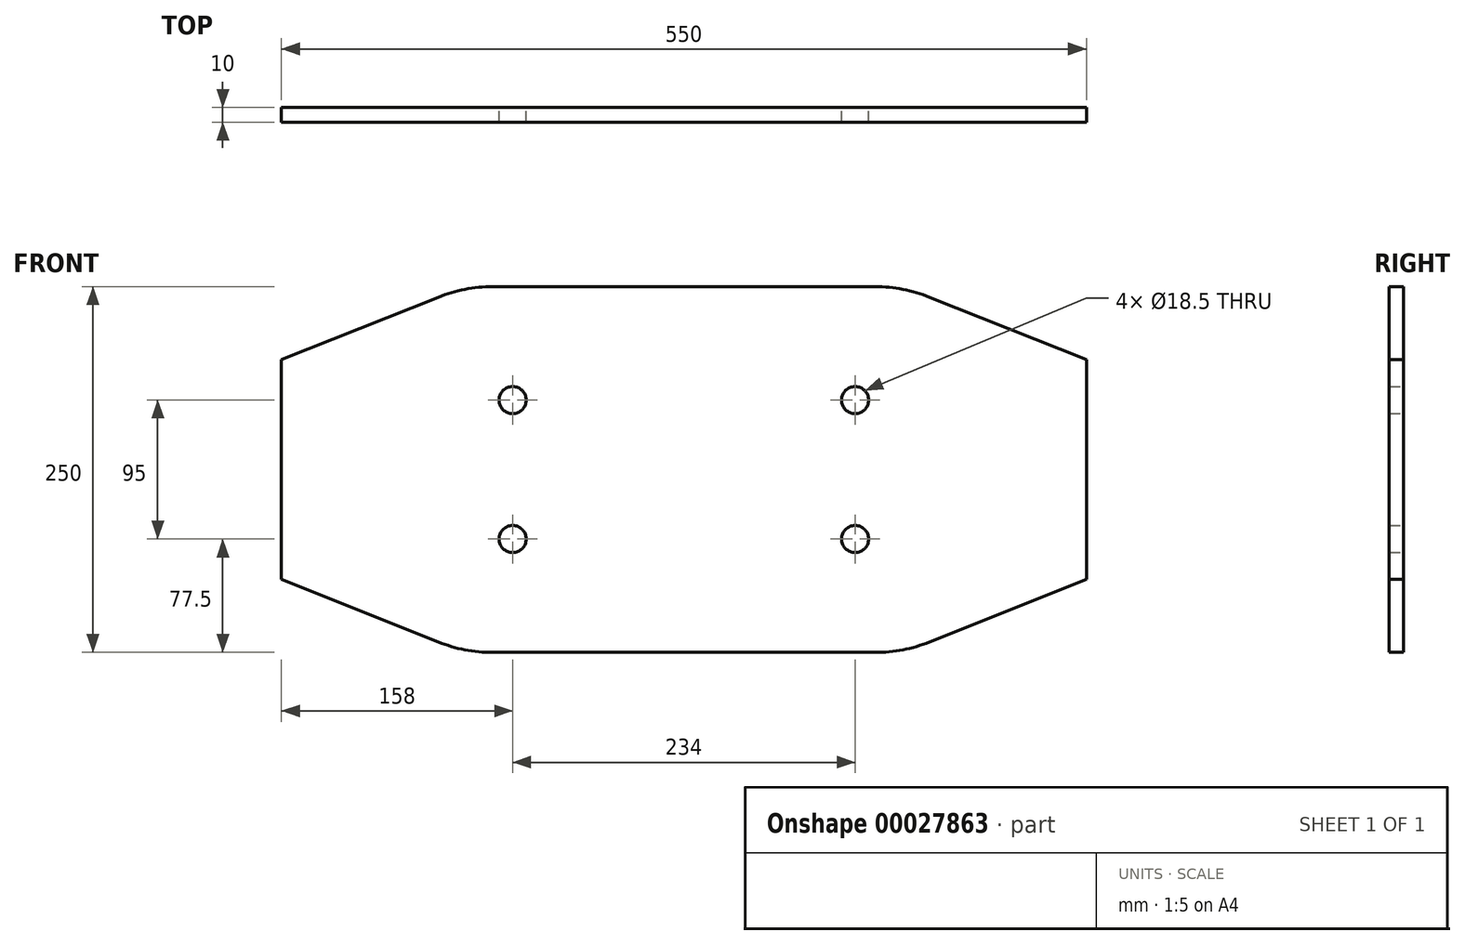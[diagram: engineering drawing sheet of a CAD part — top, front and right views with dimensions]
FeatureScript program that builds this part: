
annotation { "Feature Type Name" : "Feature", "Feature Type Description" : "" }
export const myFeature = defineFeature(function(context is Context, id is Id, definition is map)
    precondition{}
    {
        {
            var Q0;
            Q0=qCreatedBy(makeId("Front.planeOp"),FACE);
            var sketch = newSketch(context, id + "F0", { "sketchPlane" : qUnion([Q0])});
            skLineSegment(sketch, "E0", {"start": v(0, 0) * mm, "end": v(0, 150) * mm});
            skLineSegment(sketch, "E1", {"start": v(0, 150) * mm, "end": v(107.12, 192.85) * mm});
            skLineSegment(sketch, "E2", {"start": v(144.26, 200) * mm, "end": v(405.74, 200) * mm});
            skLineSegment(sketch, "E3", {"start": v(442.88, 192.85) * mm, "end": v(550, 150) * mm});
            skLineSegment(sketch, "E4", {"start": v(550, 150) * mm, "end": v(550, 0) * mm});
            skLineSegment(sketch, "E5", {"start": v(550, 0) * mm, "end": v(442.88, -42.85) * mm});
            skLineSegment(sketch, "E6", {"start": v(405.74, -50) * mm, "end": v(144.26, -50) * mm});
            skLineSegment(sketch, "E7", {"start": v(107.12, -42.85) * mm, "end": v(0, 0) * mm});
            skPoint(sketch, "E8.visualSharp", {"position": v(125, 200) * mm});
            skArc(sketch, "E8.filletArc", {"start": v(144.26, 200) * mm, "mid": v(125.35, 198.2) * mm, "end": v(107.12, 192.85) * mm});
            skPoint(sketch, "E9.visualSharp", {"position": v(425, 200) * mm});
            skArc(sketch, "E9.filletArc", {"start": v(442.88, 192.85) * mm, "mid": v(424.65, 198.2) * mm, "end": v(405.74, 200) * mm});
            skPoint(sketch, "E10.visualSharp", {"position": v(125, -50) * mm});
            skArc(sketch, "E10.filletArc", {"start": v(107.12, -42.85) * mm, "mid": v(125.35, -48.2) * mm, "end": v(144.26, -50) * mm});
            skPoint(sketch, "E11.visualSharp", {"position": v(425, -50) * mm});
            skArc(sketch, "E11.filletArc", {"start": v(405.74, -50) * mm, "mid": v(424.65, -48.2) * mm, "end": v(442.88, -42.85) * mm});
            skCircle(sketch, "E12", {"center": v(158, 122.5) * mm, "radius": 9.25 * mm});
            skCircle(sketch, "E13", {"center": v(158, 27.5) * mm, "radius": 9.25 * mm});
            skCircle(sketch, "E14", {"center": v(392, 122.5) * mm, "radius": 9.25 * mm});
            skCircle(sketch, "E15", {"center": v(392, 27.5) * mm, "radius": 9.25 * mm});
            skSolve(sketch);
        }
        {
            var Q0;
            Q0=makeQuery(id+"F0.imprint","IMPRINT",FACE,{"disambiguationData":[TD([[makeQuery(id+"F0.imprint","IMPRINT",EDGE,{"derivedFrom":sQuery(id+"F0.wireOp",EDGE,"E0")}),-1.0]])]});
            extrude(context, id + "F1", {"entities" : qUnion([Q0]), "depth" : 10 * mm});
        }
    });
